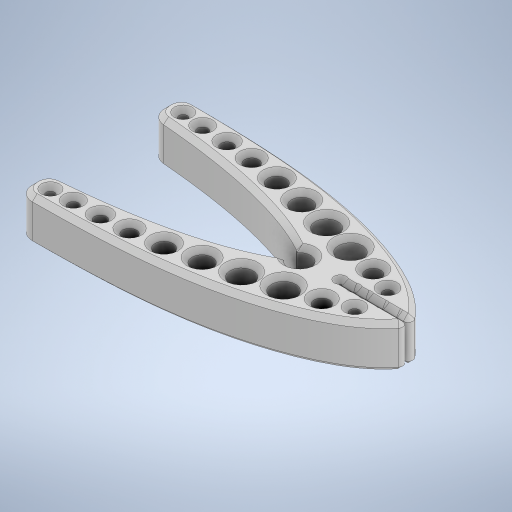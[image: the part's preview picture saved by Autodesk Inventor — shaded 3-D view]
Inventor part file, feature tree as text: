
AUTODESK INVENTOR PART (.ipt)
format: ipt  version: 2024.1 (Build 281209000, 209)  size: 704,512 bytes
history: native  units: mm
features: fillet x3, extrude x2, mirror x2, chamfer x2, sketch x2
ambient origin geometry x8: Origin, YZ Plane, XZ Plane, XY Plane, X Axis, Y Axis, Z Axis, Center Point
bodies: Solid1 (feature_tree)
feature tree (11):
  extrude  "Extrusion1"  Depth=9.0mm
  mirror  "Mirror1"
  fillet  "Fillet1"  Radius=17.0mm
  fillet  "Fillet2"  Radius=15.0mm
  fillet  "Fillet3"  Radius=8.0mm
  chamfer  "Chamfer1"  Distance=9.0mm
  extrude  "Extrusion2"  Depth=0.5mm
  chamfer  "Chamfer2"  Distance=0.3mm
  mirror  "Mirror2"
  sketch  "Sketch1"  dims[d0=0.1mm d1=65.0mm d4=0.05mm d8=17.0mm d9=15.0mm d10=8.0mm d11=9.0mm d12=0.0mm]
  sketch  "Sketch2"  dims[d13=0.15mm d14=0.5mm d15=0.3mm d16=0.2mm d17=0.4mm d18=2.0mm d19=1.0mm d20=3.0mm d21=0.999mm d22=2.0mm d23=45.0deg d26=0.0mm d27=0.0mm d28=1.0mm d29=2.0mm d30=45.0deg]
